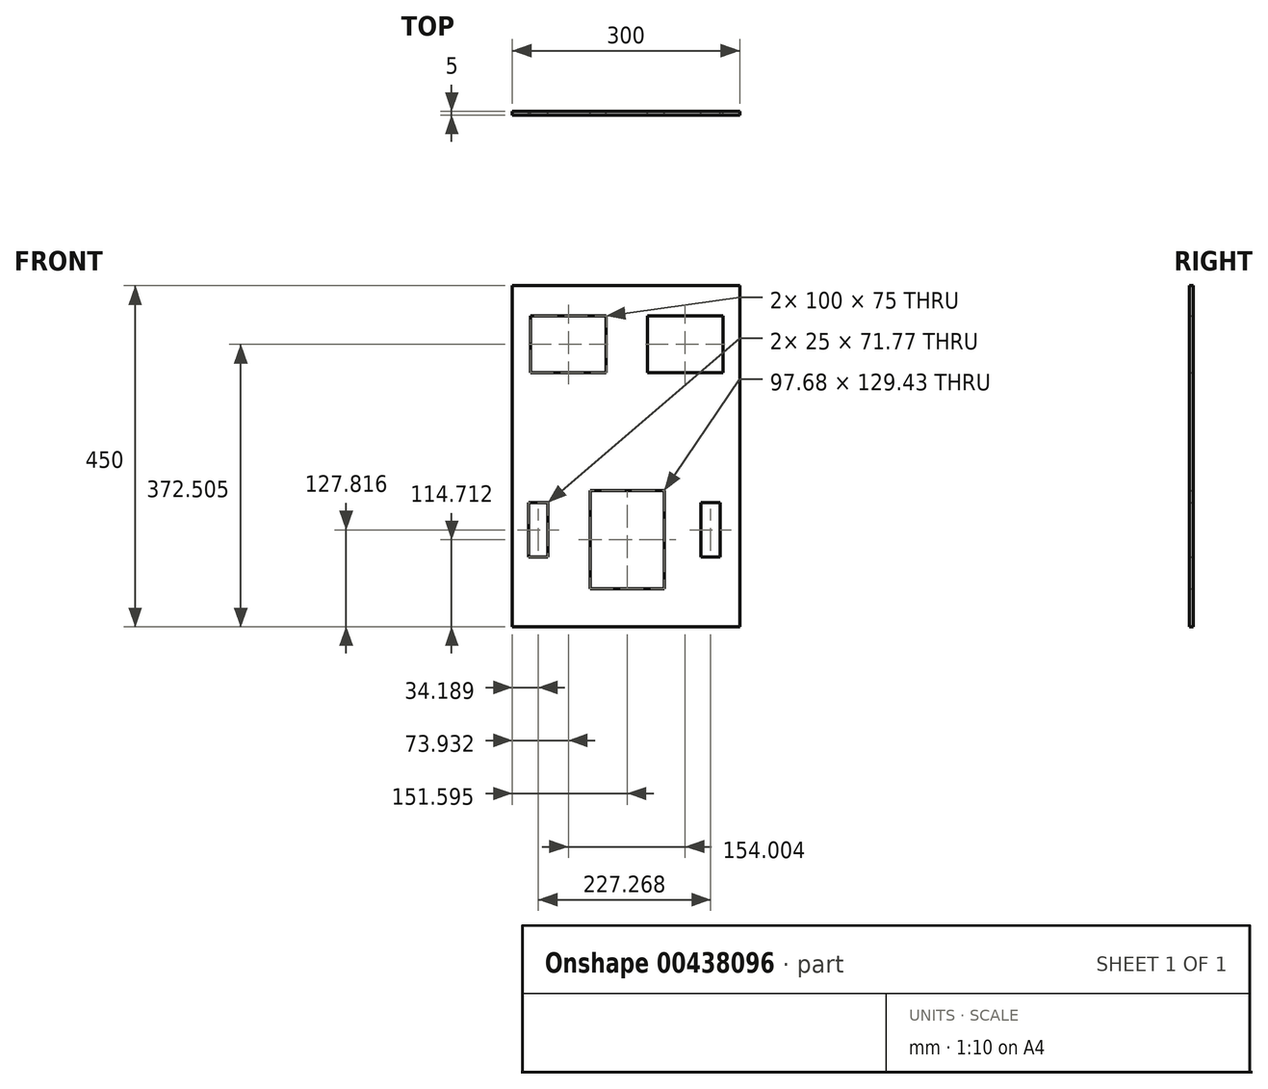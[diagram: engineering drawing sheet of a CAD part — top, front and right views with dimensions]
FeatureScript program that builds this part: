
annotation { "Feature Type Name" : "Feature", "Feature Type Description" : "" }
export const myFeature = defineFeature(function(context is Context, id is Id, definition is map)
    precondition{}
    {
        {
            var Q0;
            Q0=qCreatedBy(makeId("Front.planeOp"),FACE);
            var sketch = newSketch(context, id + "F0", { "sketchPlane" : qUnion([Q0])});
            skLineSegment(sketch, "E0.bottom", {"start": v(-285.9, 244.7) * mm, "end": v(14.1, 244.7) * mm});
            skLineSegment(sketch, "E0.top", {"start": v(-285.9, -205.3) * mm, "end": v(14.1, -205.3) * mm});
            skLineSegment(sketch, "E0.left", {"start": v(-285.9, 244.7) * mm, "end": v(-285.9, -205.3) * mm});
            skLineSegment(sketch, "E0.right", {"start": v(14.1, 244.7) * mm, "end": v(14.1, -205.3) * mm});
            skLineSegment(sketch, "E1", {"start": v(-285.9, 129.42) * mm, "end": v(-285.9, 0) * mm});
            skLineSegment(sketch, "E2", {"start": v(14.1, 69.66) * mm, "end": v(14.1, 59.76) * mm});
            skLineSegment(sketch, "E3", {"start": v(-285.9, 64.7) * mm, "end": v(14.1, 64.7) * mm});
            skLineSegment(sketch, "E4", {"start": v(14.1, 64.7) * mm, "end": v(14.1, 24.7) * mm});
            skLineSegment(sketch, "E5", {"start": v(14.1, 24.7) * mm, "end": v(-285.9, 24.7) * mm});
            skLineSegment(sketch, "E6", {"start": v(-285.9, 24.7) * mm, "end": v(-285.9, 64.7) * mm});
            skLineSegment(sketch, "E7.top", {"start": v(-77.68, -205.3) * mm, "end": v(-197.68, -205.3) * mm});
            skLineSegment(sketch, "E8.bottom", {"start": v(-36.95, -41.59) * mm, "end": v(-11.95, -41.59) * mm});
            skLineSegment(sketch, "E8.top", {"start": v(-36.95, -113.36) * mm, "end": v(-11.95, -113.36) * mm});
            skLineSegment(sketch, "E8.left", {"start": v(-36.95, -41.59) * mm, "end": v(-36.95, -113.36) * mm});
            skLineSegment(sketch, "E8.right", {"start": v(-11.95, -41.59) * mm, "end": v(-11.95, -113.36) * mm});
            skLineSegment(sketch, "E9.bottom", {"start": v(-264.22, -41.59) * mm, "end": v(-239.22, -41.59) * mm});
            skLineSegment(sketch, "E9.top", {"start": v(-264.22, -113.36) * mm, "end": v(-239.22, -113.36) * mm});
            skLineSegment(sketch, "E9.left", {"start": v(-264.22, -41.59) * mm, "end": v(-264.22, -113.36) * mm});
            skLineSegment(sketch, "E9.right", {"start": v(-239.22, -41.59) * mm, "end": v(-239.22, -113.36) * mm});
            skLineSegment(sketch, "E10.bottom", {"start": v(-261.98, 204.72) * mm, "end": v(-161.98, 204.72) * mm});
            skLineSegment(sketch, "E10.top", {"start": v(-261.98, 129.72) * mm, "end": v(-161.98, 129.72) * mm});
            skLineSegment(sketch, "E10.left", {"start": v(-261.98, 204.72) * mm, "end": v(-261.98, 129.72) * mm});
            skLineSegment(sketch, "E10.right", {"start": v(-161.98, 204.72) * mm, "end": v(-161.98, 129.72) * mm});
            skLineSegment(sketch, "E11.bottom", {"start": v(-107.97, 204.72) * mm, "end": v(-7.97, 204.72) * mm});
            skLineSegment(sketch, "E11.top", {"start": v(-107.97, 129.72) * mm, "end": v(-7.97, 129.72) * mm});
            skLineSegment(sketch, "E11.left", {"start": v(-107.97, 204.72) * mm, "end": v(-107.97, 129.72) * mm});
            skLineSegment(sketch, "E11.right", {"start": v(-7.97, 204.72) * mm, "end": v(-7.97, 129.72) * mm});
            skLineSegment(sketch, "E12", {"start": v(-285.9, -155.3) * mm, "end": v(14.1, -155.3) * mm, "construction": true});
            skLineSegment(sketch, "E13", {"start": v(-135.9, -155.3) * mm, "end": v(-135.9, -205.3) * mm, "construction": true});
            skLineSegment(sketch, "E14", {"start": v(-147.54, 24.7) * mm, "end": v(-147.54, -155.3) * mm, "construction": true});
            skLineSegment(sketch, "E15", {"start": v(-144.46, 244.7) * mm, "end": v(-144.46, 64.7) * mm, "construction": true});
            skLineSegment(sketch, "E16.bottom", {"start": v(-183.16, -155.3) * mm, "end": v(-85.48, -155.3) * mm});
            skLineSegment(sketch, "E16.top", {"start": v(-183.16, -25.86) * mm, "end": v(-85.48, -25.86) * mm});
            skLineSegment(sketch, "E16.left", {"start": v(-183.16, -155.3) * mm, "end": v(-183.16, -25.86) * mm});
            skLineSegment(sketch, "E16.right", {"start": v(-85.48, -155.3) * mm, "end": v(-85.48, -25.86) * mm});
            skLineSegment(sketch, "E17", {"start": v(-134.32, -25.86) * mm, "end": v(-135.9, -161.34) * mm});
            skSolve(sketch);
        }
        {
            var Q0;
            {var subQ1=sQuery(id+"F0.wireOp",EDGE,"E0.bottom");Q0=makeQuery(id+"F0.imprint","IMPRINT",FACE,{"disambiguationData":[TD([[makeQuery(id+"F0.imprint","IMPRINT",EDGE,{"derivedFrom":subQ1}),-1.0]])]});}
            var Q1;
            {var subQ0=sQuery(id+"F0.wireOp",EDGE,"E3");Q1=makeQuery(id+"F0.imprint","IMPRINT",FACE,{"disambiguationData":[TD([[makeQuery(id+"F0.imprint","IMPRINT",EDGE,{"derivedFrom":subQ0}),-1.0]])]});}
            var Q2;
            {var subQ4=sQuery(id+"F0.wireOp",EDGE,"E5");Q2=makeQuery(id+"F0.imprint","IMPRINT",FACE,{"disambiguationData":[TD([[makeQuery(id+"F0.imprint","IMPRINT",EDGE,{"derivedFrom":subQ4}),1.0]])]});}
            extrude(context, id + "F1", {"entities" : qUnion([Q0, Q1, Q2]), "depth" : 5 * mm});
        }
    });
